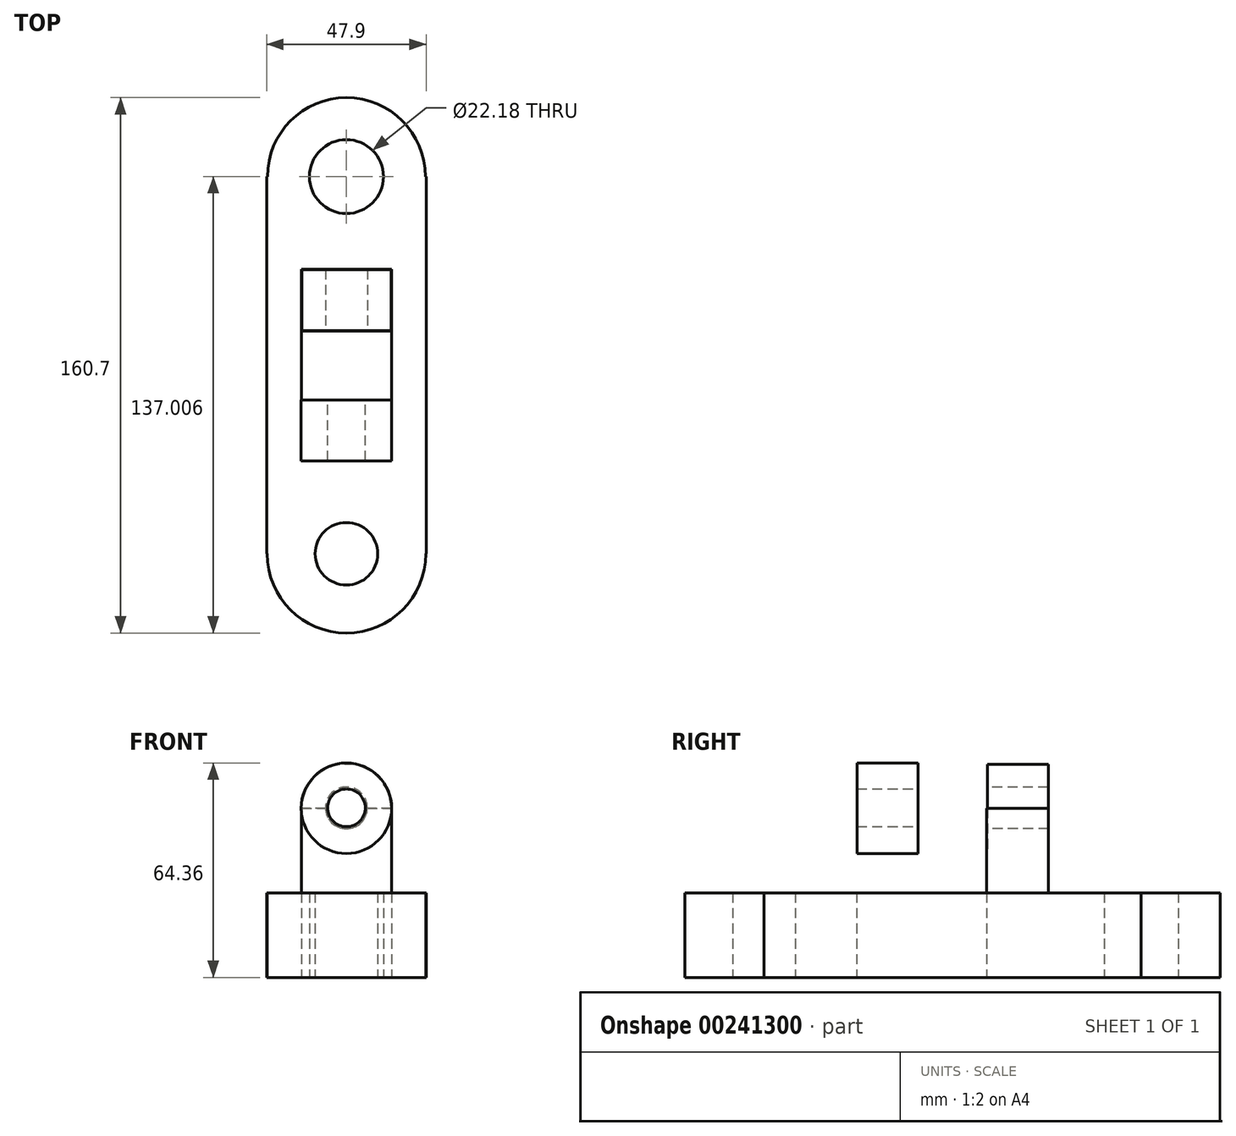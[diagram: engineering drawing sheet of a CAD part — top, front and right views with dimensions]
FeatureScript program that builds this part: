
annotation { "Feature Type Name" : "Feature", "Feature Type Description" : "" }
export const myFeature = defineFeature(function(context is Context, id is Id, definition is map)
    precondition{}
    {
        {
            var Q0;
            Q0=qCreatedBy(makeId("Top.planeOp"),FACE);
            var sketch = newSketch(context, id + "F0", { "sketchPlane" : qUnion([Q0])});
            skLineSegment(sketch, "E0.bottom", {"start": v(23.95, -56.6) * mm, "end": v(23.8, -56.6) * mm});
            skLineSegment(sketch, "E0.top", {"start": v(23.95, 56.6) * mm, "end": v(23.7, 56.6) * mm});
            skLineSegment(sketch, "E0.left", {"start": v(23.95, -56.6) * mm, "end": v(23.95, 56.6) * mm});
            skLineSegment(sketch, "E0.right", {"start": v(-23.95, -56.6) * mm, "end": v(-23.95, 56.6) * mm});
            skPoint(sketch, "E0.middle", {"position": v(0, 0) * mm});
            skArc(sketch, "E1", {"start": v(23.7, 56.6) * mm, "mid": v(0, 80.3) * mm, "end": v(-23.7, 56.6) * mm});
            skArc(sketch, "E2", {"start": v(-23.8, -56.6) * mm, "mid": v(0, -80.4) * mm, "end": v(23.8, -56.6) * mm});
            skLineSegment(sketch, "E3.trimOffspring", {"start": v(-23.7, 56.6) * mm, "end": v(-23.95, 56.6) * mm});
            skLineSegment(sketch, "E4.trimOffspring", {"start": v(-23.8, -56.6) * mm, "end": v(-23.95, -56.6) * mm});
            skCircle(sketch, "E5", {"center": v(0, -56.6) * mm, "radius": 9.38 * mm});
            skCircle(sketch, "E6", {"center": v(0, 56.6) * mm, "radius": 11.1 * mm});
            skLineSegment(sketch, "E7.bottom", {"start": v(13.54, 28.77) * mm, "end": v(-13.54, 28.77) * mm});
            skLineSegment(sketch, "E7.top", {"start": v(13.54, -28.77) * mm, "end": v(-13.54, -28.77) * mm});
            skLineSegment(sketch, "E7.left", {"start": v(13.54, 28.77) * mm, "end": v(13.54, -28.77) * mm});
            skLineSegment(sketch, "E7.right", {"start": v(-13.54, 28.77) * mm, "end": v(-13.54, -28.77) * mm});
            skLineSegment(sketch, "E8.top", {"start": v(13.54, 10.22) * mm, "end": v(-13.54, 10.22) * mm});
            skLineSegment(sketch, "E8.left", {"start": v(13.54, 28.77) * mm, "end": v(13.54, 10.22) * mm});
            skLineSegment(sketch, "E8.right", {"start": v(-13.54, 28.77) * mm, "end": v(-13.54, 10.22) * mm});
            skPoint(sketch, "E8.middle", {"position": v(0, 19.5) * mm});
            skLineSegment(sketch, "E9.top", {"start": v(13.54, -10.22) * mm, "end": v(-13.54, -10.22) * mm});
            skLineSegment(sketch, "E9.left", {"start": v(13.54, -28.77) * mm, "end": v(13.54, -10.22) * mm});
            skLineSegment(sketch, "E9.right", {"start": v(-13.54, -28.77) * mm, "end": v(-13.54, -10.22) * mm});
            skPoint(sketch, "E9.middle", {"position": v(0, -19.5) * mm});
            skSolve(sketch);
        }
        {
            var Q0;
            Q0=makeQuery(id+"F0.imprint","IMPRINT",FACE,{"disambiguationData":[TD([[makeQuery(id+"F0.imprint","IMPRINT",EDGE,{"derivedFrom":sQuery(id+"F0.wireOp",EDGE,"E7.top")}),-1.0]])]});
            var Q1;
            Q1=makeQuery(id+"F0.imprint","IMPRINT",FACE,{"disambiguationData":[TD([[makeQuery(id+"F0.imprint","IMPRINT",EDGE,{"derivedFrom":sQuery(id+"F0.wireOp",EDGE,"E7.bottom")}),1.0]])]});
            extrude(context, id + "F1", {"entities" : qUnion([Q0, Q1]), "depth" : 50.8 * mm});
        }
        {
            var Q0;
            Q0 = qSketchRegion(id + "F0", true);
            extrude(context, id + "F2", {"entities" : qUnion([Q0]), "operationType" : NewBodyOperationType.ADD, "depth" : 25.4 * mm});
        }
        {
            var Q0;
            Q0=qCreatedBy(makeId("Front.planeOp"),FACE);
            var sketch = newSketch(context, id + "F3", { "sketchPlane" : qUnion([Q0])});
            skCircle(sketch, "E10", {"center": v(0, 50.77) * mm, "radius": 13.59 * mm});
            skSolve(sketch);
        }
        {
            var Q0;
            Q0 = qSketchRegion(id + "F3", true);
            extrude(context, id + "F4", {"entities" : qUnion([Q0]), "operationType" : NewBodyOperationType.ADD, "depth" : 25.4 * mm});
        }
        {
            var Q0;
            Q0 = qSketchRegion(id + "F3", true);
            extrude(context, id + "F5", {"entities" : qUnion([Q0]), "operationType" : NewBodyOperationType.ADD, "depth" : 13.2 * mm});
        }
        {
            var Q0;
            Q0=makeQuery(id+"F4.opExtrude","CAP_FACE",FACE,{"disambiguationData":[OSD([sQuery(id+"F3.wireOp",EDGE,"E10")])],"isStart":false});
            extrude(context, id + "F6", {"entities" : qUnion([Q0]), "operationType" : NewBodyOperationType.ADD, "depth" : 3.3 * mm});
        }
        {
            var Q0;
            Q0=makeQuery(id+"F4.opExtrude","CAP_FACE",FACE,{"disambiguationData":[OSD([sQuery(id+"F3.wireOp",EDGE,"E10")])],"isStart":true});
            extrude(context, id + "F7", {"entities" : qUnion([Q0]), "operationType" : NewBodyOperationType.REMOVE, "oppositeDirection" : true, "depth" : 10.4 * mm});
        }
        {
            var Q0;
            Q0=qCreatedBy(makeId("Front.planeOp"),FACE);
            var sketch = newSketch(context, id + "F8", { "sketchPlane" : qUnion([Q0])});
            skCircle(sketch, "E11", {"center": v(0, 50.62) * mm, "radius": 13.4 * mm});
            skSolve(sketch);
        }
        {
            var Q0;
            Q0=makeQuery(id+"F8.imprint","IMPRINT",FACE,{"disambiguationData":[TD([[makeQuery(id+"F8.imprint","IMPRINT",EDGE,{"derivedFrom":sQuery(id+"F8.wireOp",EDGE,"E11")}),1.0]])]});
            extrude(context, id + "F9", {"entities" : qUnion([Q0]), "operationType" : NewBodyOperationType.ADD, "oppositeDirection" : true, "depth" : 28.7 * mm});
        }
        {
            var Q0;
            Q0=makeQuery(id+"F9.opExtrude","CAP_FACE",FACE,{"disambiguationData":[OSD([sQuery(id+"F8.wireOp",EDGE,"E11")])],"isStart":true});
            extrude(context, id + "F10", {"entities" : qUnion([Q0]), "operationType" : NewBodyOperationType.REMOVE, "oppositeDirection" : true, "depth" : 10.4 * mm});
        }
        {
            var Q0;
            Q0=qCreatedBy(makeId("Front.planeOp"),FACE);
            var sketch = newSketch(context, id + "F11", { "sketchPlane" : qUnion([Q0])});
            skCircle(sketch, "E12", {"center": v(0, 50.9) * mm, "radius": 6.27 * mm});
            skSolve(sketch);
        }
        {
            var Q0;
            Q0=makeQuery(id+"F11.imprint","IMPRINT",FACE,{"disambiguationData":[TD([[makeQuery(id+"F11.imprint","IMPRINT",EDGE,{"derivedFrom":sQuery(id+"F11.wireOp",EDGE,"E12")}),1.0]])]});
            extrude(context, id + "F12", {"entities" : qUnion([Q0]), "operationType" : NewBodyOperationType.REMOVE, "oppositeDirection" : true, "depth" : 36.32 * mm});
        }
        {
            var Q0;
            Q0=qCreatedBy(makeId("Front.planeOp"),FACE);
            var sketch = newSketch(context, id + "F13", { "sketchPlane" : qUnion([Q0])});
            skCircle(sketch, "E13", {"center": v(0, 50.9) * mm, "radius": 5.66 * mm});
            skSolve(sketch);
        }
        {
            var Q0;
            Q0=makeQuery(id+"F13.imprint","IMPRINT",FACE,{"disambiguationData":[TD([[makeQuery(id+"F13.imprint","IMPRINT",EDGE,{"derivedFrom":sQuery(id+"F13.wireOp",EDGE,"E13")}),1.0]])]});
            extrude(context, id + "F14", {"entities" : qUnion([Q0]), "operationType" : NewBodyOperationType.REMOVE, "depth" : 82.04 * mm});
        }
    });
